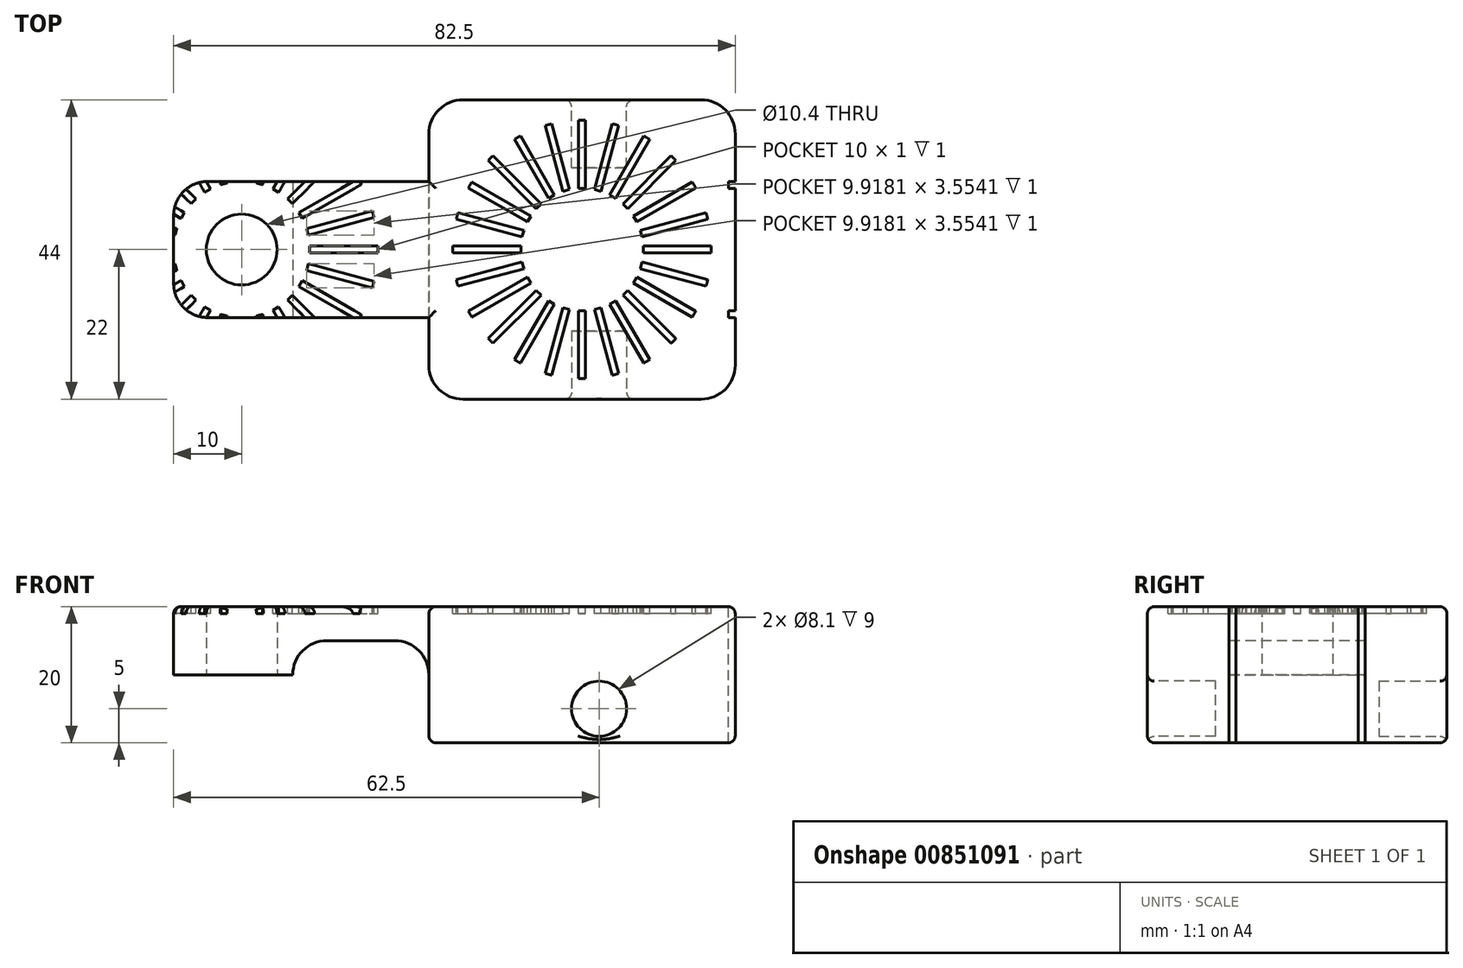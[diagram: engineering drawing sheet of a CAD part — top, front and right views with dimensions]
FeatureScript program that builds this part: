
annotation { "Feature Type Name" : "Feature", "Feature Type Description" : "" }
export const myFeature = defineFeature(function(context is Context, id is Id, definition is map)
    precondition{}
    {
        {
            var Q0;
            Q0=qCreatedBy(makeId("Top.planeOp"),FACE);
            var sketch = newSketch(context, id + "F0", { "sketchPlane" : qUnion([Q0])});
            skLineSegment(sketch, "E0.bottom", {"start": v(17.5, -22) * mm, "end": v(-17.5, -22) * mm});
            skLineSegment(sketch, "E0.top", {"start": v(17.5, 22) * mm, "end": v(-17.5, 22) * mm});
            skLineSegment(sketch, "E0.left", {"start": v(22.5, -17) * mm, "end": v(22.5, 17) * mm});
            skLineSegment(sketch, "E0.right", {"start": v(-22.5, -17) * mm, "end": v(-22.5, -10) * mm});
            skPoint(sketch, "E0.middle", {"position": v(0, 0) * mm});
            skPoint(sketch, "E1.visualSharp", {"position": v(-22.5, -22) * mm});
            skArc(sketch, "E1.filletArc", {"start": v(-22.5, -17) * mm, "mid": v(-21.04, -20.54) * mm, "end": v(-17.5, -22) * mm});
            skPoint(sketch, "E2.visualSharp", {"position": v(-22.5, 22) * mm});
            skArc(sketch, "E2.filletArc", {"start": v(-17.5, 22) * mm, "mid": v(-21.04, 20.54) * mm, "end": v(-22.5, 17) * mm});
            skPoint(sketch, "E3.visualSharp", {"position": v(22.5, 22) * mm});
            skArc(sketch, "E3.filletArc", {"start": v(22.5, 17) * mm, "mid": v(21.04, 20.54) * mm, "end": v(17.5, 22) * mm});
            skPoint(sketch, "E4.visualSharp", {"position": v(22.5, -22) * mm});
            skArc(sketch, "E4.filletArc", {"start": v(17.5, -22) * mm, "mid": v(21.04, -20.54) * mm, "end": v(22.5, -17) * mm});
            skLineSegment(sketch, "E5.bottom", {"start": v(-22.5, -10) * mm, "end": v(-55, -10) * mm});
            skLineSegment(sketch, "E5.top", {"start": v(-22.5, 10) * mm, "end": v(-55, 10) * mm});
            skLineSegment(sketch, "E5.right", {"start": v(-60, -5) * mm, "end": v(-60, 5) * mm});
            skCircle(sketch, "E6", {"center": v(-50, 0) * mm, "radius": 5.2 * mm});
            skPoint(sketch, "E7.orphan", {"position": v(0, -10) * mm});
            skLineSegment(sketch, "E8.trimOffspring", {"start": v(-22.5, 10) * mm, "end": v(-22.5, 17) * mm});
            skPoint(sketch, "E9.visualSharp", {"position": v(-60, -10) * mm});
            skArc(sketch, "E9.filletArc", {"start": v(-60, -5) * mm, "mid": v(-58.54, -8.54) * mm, "end": v(-55, -10) * mm});
            skPoint(sketch, "E10.visualSharp", {"position": v(-60, 10) * mm});
            skArc(sketch, "E10.filletArc", {"start": v(-55, 10) * mm, "mid": v(-58.54, 8.54) * mm, "end": v(-60, 5) * mm});
            skSolve(sketch);
        }
        {
            var Q0;
            Q0 = qSketchRegion(id + "F0", true);
            extrude(context, id + "F1", {"entities" : qUnion([Q0]), "depth" : 20 * mm, "offsetDistance" : 25 * mm});
        }
        {
            var Q0;
            Q0=makeQuery(id+"F1.opExtrude","CAP_FACE",FACE,{"disambiguationData":[OSD([sQuery(id+"F0.wireOp",EDGE,"E0.bottom"),sQuery(id+"F0.wireOp",EDGE,"E0.top"),sQuery(id+"F0.wireOp",EDGE,"E0.left"),sQuery(id+"F0.wireOp",EDGE,"E0.right"),sQuery(id+"F0.wireOp",EDGE,"E1.filletArc"),sQuery(id+"F0.wireOp",EDGE,"E2.filletArc"),sQuery(id+"F0.wireOp",EDGE,"E3.filletArc"),sQuery(id+"F0.wireOp",EDGE,"E4.filletArc"),sQuery(id+"F0.wireOp",EDGE,"E5.bottom"),sQuery(id+"F0.wireOp",EDGE,"E5.top"),sQuery(id+"F0.wireOp",EDGE,"E5.right"),sQuery(id+"F0.wireOp",EDGE,"E6"),sQuery(id+"F0.wireOp",EDGE,"E8.trimOffspring"),sQuery(id+"F0.wireOp",EDGE,"E9.filletArc"),sQuery(id+"F0.wireOp",EDGE,"E10.filletArc")])],"isStart":true});
            var sketch = newSketch(context, id + "F2", { "sketchPlane" : qUnion([Q0])});
            skLineSegment(sketch, "E11.bottom", {"start": v(-22.5, 10) * mm, "end": v(-60, 10) * mm});
            skLineSegment(sketch, "E11.top", {"start": v(-22.5, -10) * mm, "end": v(-60, -10) * mm});
            skLineSegment(sketch, "E11.left", {"start": v(-22.5, 10) * mm, "end": v(-22.5, -10) * mm});
            skLineSegment(sketch, "E11.right", {"start": v(-60, 10) * mm, "end": v(-60, -10) * mm});
            skSolve(sketch);
        }
        {
            var Q0;
            Q0 = qSketchRegion(id + "F2", true);
            extrude(context, id + "F3", {"entities" : qUnion([Q0]), "operationType" : NewBodyOperationType.REMOVE, "oppositeDirection" : true, "depth" : 10 * mm, "offsetDistance" : 25 * mm});
        }
        {
            var Q0;
            Q0=makeQuery(id+"F1.opExtrude","SWEPT_FACE",FACE,{"disambiguationData":[OSD([sQuery(id+"F0.wireOp",EDGE,"E0.bottom")])]});
            var sketch = newSketch(context, id + "F4", { "sketchPlane" : qUnion([Q0])});
            skCircle(sketch, "E12", {"center": v(2.5, 5) * mm, "radius": 4.05 * mm});
            skSolve(sketch);
        }
        {
            var Q0;
            Q0 = qSketchRegion(id + "F4", true);
            extrude(context, id + "F5", {"entities" : qUnion([Q0]), "operationType" : NewBodyOperationType.REMOVE, "oppositeDirection" : true, "depth" : 10 * mm, "offsetDistance" : 25 * mm});
        }
        {
            var Q0;
            Q0=makeQuery(id+"F1.opExtrude","SWEPT_FACE",FACE,{"disambiguationData":[OSD([sQuery(id+"F0.wireOp",EDGE,"E0.top")])]});
            var sketch = newSketch(context, id + "F6", { "sketchPlane" : qUnion([Q0])});
            skCircle(sketch, "E13", {"center": v(-2.5, 5) * mm, "radius": 4.05 * mm});
            skSolve(sketch);
        }
        {
            var Q0;
            Q0 = qSketchRegion(id + "F6", true);
            extrude(context, id + "F7", {"entities" : qUnion([Q0]), "operationType" : NewBodyOperationType.REMOVE, "oppositeDirection" : true, "depth" : 10 * mm, "offsetDistance" : 25 * mm});
        }
        {
            var Q0;
            Q0=makeQuery(id+"F1.opExtrude","CAP_FACE",FACE,{"disambiguationData":[OSD([sQuery(id+"F0.wireOp",EDGE,"E0.bottom"),sQuery(id+"F0.wireOp",EDGE,"E0.top"),sQuery(id+"F0.wireOp",EDGE,"E0.left"),sQuery(id+"F0.wireOp",EDGE,"E0.right"),sQuery(id+"F0.wireOp",EDGE,"E1.filletArc"),sQuery(id+"F0.wireOp",EDGE,"E2.filletArc"),sQuery(id+"F0.wireOp",EDGE,"E3.filletArc"),sQuery(id+"F0.wireOp",EDGE,"E4.filletArc"),sQuery(id+"F0.wireOp",EDGE,"E5.bottom"),sQuery(id+"F0.wireOp",EDGE,"E5.top"),sQuery(id+"F0.wireOp",EDGE,"E5.right"),sQuery(id+"F0.wireOp",EDGE,"E6"),sQuery(id+"F0.wireOp",EDGE,"E8.trimOffspring"),sQuery(id+"F0.wireOp",EDGE,"E9.filletArc"),sQuery(id+"F0.wireOp",EDGE,"E10.filletArc")])],"isStart":true});
            var Q1;
            Q1=makeQuery(id+"F3.boolean.opBoolean","COPY",EDGE,{"derivedFrom":makeQuery(id+"F3.opExtrude","CAP_EDGE",EDGE,{"disambiguationData":[OSD([sQuery(id+"F2.wireOp",EDGE,"E11.right")])],"isStart":false})});
            var Q2;
            Q2=makeQuery(id+"F1.opExtrude","CAP_EDGE",EDGE,{"disambiguationData":[OSD([sQuery(id+"F0.wireOp",EDGE,"E5.bottom")])],"isStart":false});
            var Q3;
            Q3=makeQuery(id+"F1.opExtrude","CAP_EDGE",EDGE,{"disambiguationData":[OSD([sQuery(id+"F0.wireOp",EDGE,"E0.top")])],"isStart":false});
            var Q4;
            Q4=makeQuery(id+"F1.opExtrude","SWEPT_FACE",FACE,{"disambiguationData":[OSD([sQuery(id+"F0.wireOp",EDGE,"E0.bottom")])]});
            var Q5;
            Q5=makeQuery(id+"F1.opExtrude","SWEPT_FACE",FACE,{"disambiguationData":[OSD([sQuery(id+"F0.wireOp",EDGE,"E0.top")])]});
            fillet(context, id + "F8", {"entities" : qUnion([Q0, Q1, Q2, Q3, Q4, Q5]), "radius" : 1 * mm, "tangentPropagation" : true, "allowEdgeOverflow" : false});
        }
        {
            var Q0;
            Q0=makeQuery(id+"F1.opExtrude","CAP_FACE",FACE,{"disambiguationData":[OSD([sQuery(id+"F0.wireOp",EDGE,"E0.bottom"),sQuery(id+"F0.wireOp",EDGE,"E0.top"),sQuery(id+"F0.wireOp",EDGE,"E0.left"),sQuery(id+"F0.wireOp",EDGE,"E0.right"),sQuery(id+"F0.wireOp",EDGE,"E1.filletArc"),sQuery(id+"F0.wireOp",EDGE,"E2.filletArc"),sQuery(id+"F0.wireOp",EDGE,"E3.filletArc"),sQuery(id+"F0.wireOp",EDGE,"E4.filletArc"),sQuery(id+"F0.wireOp",EDGE,"E5.bottom"),sQuery(id+"F0.wireOp",EDGE,"E5.top"),sQuery(id+"F0.wireOp",EDGE,"E5.right"),sQuery(id+"F0.wireOp",EDGE,"E6"),sQuery(id+"F0.wireOp",EDGE,"E8.trimOffspring"),sQuery(id+"F0.wireOp",EDGE,"E9.filletArc"),sQuery(id+"F0.wireOp",EDGE,"E10.filletArc")])],"isStart":false});
            var sketch = newSketch(context, id + "F9", { "sketchPlane" : qUnion([Q0])});
            skArc(sketch, "E14", {"start": v(19, -0.5) * mm, "mid": v(19, 0) * mm, "end": v(19, 0.5) * mm});
            skLineSegment(sketch, "E15.bottom", {"start": v(19, 0.5) * mm, "end": v(9, 0.5) * mm});
            skLineSegment(sketch, "E15.top", {"start": v(19, -0.5) * mm, "end": v(9, -0.5) * mm});
            skLineSegment(sketch, "E15.right", {"start": v(9, 0.5) * mm, "end": v(9, -0.5) * mm});
            skLineSegment(sketch, "E16.1.0", {"start": v(18.48, 4.43) * mm, "end": v(8.82, 1.84) * mm});
            skLineSegment(sketch, "E16.1.1", {"start": v(18.22, 5.4) * mm, "end": v(8.56, 2.81) * mm});
            skLineSegment(sketch, "E16.1.2", {"start": v(8.56, 2.81) * mm, "end": v(8.82, 1.84) * mm});
            skArc(sketch, "E16.1.3", {"start": v(18.48, 4.43) * mm, "mid": v(18.35, 4.92) * mm, "end": v(18.22, 5.4) * mm});
            skLineSegment(sketch, "E16.2.0", {"start": v(16.7, 9.06) * mm, "end": v(8.04, 4.06) * mm});
            skLineSegment(sketch, "E16.2.1", {"start": v(16.2, 9.93) * mm, "end": v(7.54, 4.93) * mm});
            skLineSegment(sketch, "E16.2.2", {"start": v(7.54, 4.93) * mm, "end": v(8.04, 4.06) * mm});
            skArc(sketch, "E16.2.3", {"start": v(16.7, 9.06) * mm, "mid": v(16.45, 9.5) * mm, "end": v(16.2, 9.93) * mm});
            skLineSegment(sketch, "E16.3.0", {"start": v(13.78, 13.08) * mm, "end": v(6.71, 6) * mm});
            skLineSegment(sketch, "E16.3.1", {"start": v(13.08, 13.78) * mm, "end": v(6, 6.71) * mm});
            skLineSegment(sketch, "E16.3.2", {"start": v(6, 6.71) * mm, "end": v(6.71, 6) * mm});
            skArc(sketch, "E16.3.3", {"start": v(13.78, 13.08) * mm, "mid": v(13.44, 13.44) * mm, "end": v(13.08, 13.78) * mm});
            skLineSegment(sketch, "E16.4.0", {"start": v(9.93, 16.2) * mm, "end": v(4.93, 7.54) * mm});
            skLineSegment(sketch, "E16.4.1", {"start": v(9.06, 16.7) * mm, "end": v(4.06, 8.04) * mm});
            skLineSegment(sketch, "E16.4.2", {"start": v(4.06, 8.04) * mm, "end": v(4.93, 7.54) * mm});
            skArc(sketch, "E16.4.3", {"start": v(9.93, 16.2) * mm, "mid": v(9.5, 16.45) * mm, "end": v(9.06, 16.7) * mm});
            skLineSegment(sketch, "E16.5.0", {"start": v(5.4, 18.22) * mm, "end": v(2.81, 8.56) * mm});
            skLineSegment(sketch, "E16.5.1", {"start": v(4.43, 18.48) * mm, "end": v(1.84, 8.82) * mm});
            skLineSegment(sketch, "E16.5.2", {"start": v(1.84, 8.82) * mm, "end": v(2.81, 8.56) * mm});
            skArc(sketch, "E16.5.3", {"start": v(5.4, 18.22) * mm, "mid": v(4.92, 18.35) * mm, "end": v(4.43, 18.48) * mm});
            skLineSegment(sketch, "E16.6.0", {"start": v(0.5, 19) * mm, "end": v(0.5, 9) * mm});
            skLineSegment(sketch, "E16.6.1", {"start": v(-0.5, 19) * mm, "end": v(-0.5, 9) * mm});
            skLineSegment(sketch, "E16.6.2", {"start": v(-0.5, 9) * mm, "end": v(0.5, 9) * mm});
            skArc(sketch, "E16.6.3", {"start": v(0.5, 19) * mm, "mid": v(0, 19) * mm, "end": v(-0.5, 19) * mm});
            skLineSegment(sketch, "E16.7.0", {"start": v(-4.43, 18.48) * mm, "end": v(-1.84, 8.82) * mm});
            skLineSegment(sketch, "E16.7.1", {"start": v(-5.4, 18.22) * mm, "end": v(-2.81, 8.56) * mm});
            skLineSegment(sketch, "E16.7.2", {"start": v(-2.81, 8.56) * mm, "end": v(-1.84, 8.82) * mm});
            skArc(sketch, "E16.7.3", {"start": v(-4.43, 18.48) * mm, "mid": v(-4.92, 18.35) * mm, "end": v(-5.4, 18.22) * mm});
            skLineSegment(sketch, "E16.8.0", {"start": v(-9.06, 16.7) * mm, "end": v(-4.06, 8.04) * mm});
            skLineSegment(sketch, "E16.8.1", {"start": v(-9.93, 16.2) * mm, "end": v(-4.93, 7.54) * mm});
            skLineSegment(sketch, "E16.8.2", {"start": v(-4.93, 7.54) * mm, "end": v(-4.06, 8.04) * mm});
            skArc(sketch, "E16.8.3", {"start": v(-9.06, 16.7) * mm, "mid": v(-9.5, 16.45) * mm, "end": v(-9.93, 16.2) * mm});
            skLineSegment(sketch, "E16.9.0", {"start": v(-13.08, 13.78) * mm, "end": v(-6, 6.71) * mm});
            skLineSegment(sketch, "E16.9.1", {"start": v(-13.78, 13.08) * mm, "end": v(-6.71, 6) * mm});
            skLineSegment(sketch, "E16.9.2", {"start": v(-6.71, 6) * mm, "end": v(-6, 6.71) * mm});
            skArc(sketch, "E16.9.3", {"start": v(-13.08, 13.78) * mm, "mid": v(-13.44, 13.44) * mm, "end": v(-13.78, 13.08) * mm});
            skLineSegment(sketch, "E16.10.0", {"start": v(-16.2, 9.93) * mm, "end": v(-7.54, 4.93) * mm});
            skLineSegment(sketch, "E16.10.1", {"start": v(-16.7, 9.06) * mm, "end": v(-8.04, 4.06) * mm});
            skLineSegment(sketch, "E16.10.2", {"start": v(-8.04, 4.06) * mm, "end": v(-7.54, 4.93) * mm});
            skArc(sketch, "E16.10.3", {"start": v(-16.2, 9.93) * mm, "mid": v(-16.45, 9.5) * mm, "end": v(-16.7, 9.06) * mm});
            skLineSegment(sketch, "E16.11.0", {"start": v(-18.22, 5.4) * mm, "end": v(-8.56, 2.81) * mm});
            skLineSegment(sketch, "E16.11.1", {"start": v(-18.48, 4.43) * mm, "end": v(-8.82, 1.84) * mm});
            skLineSegment(sketch, "E16.11.2", {"start": v(-8.82, 1.84) * mm, "end": v(-8.56, 2.81) * mm});
            skArc(sketch, "E16.11.3", {"start": v(-18.22, 5.4) * mm, "mid": v(-18.35, 4.92) * mm, "end": v(-18.48, 4.43) * mm});
            skLineSegment(sketch, "E16.12.0", {"start": v(-19, 0.5) * mm, "end": v(-9, 0.5) * mm});
            skLineSegment(sketch, "E16.12.1", {"start": v(-19, -0.5) * mm, "end": v(-9, -0.5) * mm});
            skLineSegment(sketch, "E16.12.2", {"start": v(-9, -0.5) * mm, "end": v(-9, 0.5) * mm});
            skArc(sketch, "E16.12.3", {"start": v(-19, 0.5) * mm, "mid": v(-19, 0) * mm, "end": v(-19, -0.5) * mm});
            skLineSegment(sketch, "E16.13.0", {"start": v(-18.48, -4.43) * mm, "end": v(-8.82, -1.84) * mm});
            skLineSegment(sketch, "E16.13.1", {"start": v(-18.22, -5.4) * mm, "end": v(-8.56, -2.81) * mm});
            skLineSegment(sketch, "E16.13.2", {"start": v(-8.56, -2.81) * mm, "end": v(-8.82, -1.84) * mm});
            skArc(sketch, "E16.13.3", {"start": v(-18.48, -4.43) * mm, "mid": v(-18.35, -4.92) * mm, "end": v(-18.22, -5.4) * mm});
            skLineSegment(sketch, "E16.14.0", {"start": v(-16.7, -9.06) * mm, "end": v(-8.04, -4.06) * mm});
            skLineSegment(sketch, "E16.14.1", {"start": v(-16.2, -9.93) * mm, "end": v(-7.54, -4.93) * mm});
            skLineSegment(sketch, "E16.14.2", {"start": v(-7.54, -4.93) * mm, "end": v(-8.04, -4.06) * mm});
            skArc(sketch, "E16.14.3", {"start": v(-16.7, -9.06) * mm, "mid": v(-16.45, -9.5) * mm, "end": v(-16.2, -9.93) * mm});
            skLineSegment(sketch, "E16.15.0", {"start": v(-13.78, -13.08) * mm, "end": v(-6.71, -6) * mm});
            skLineSegment(sketch, "E16.15.1", {"start": v(-13.08, -13.78) * mm, "end": v(-6, -6.71) * mm});
            skLineSegment(sketch, "E16.15.2", {"start": v(-6, -6.71) * mm, "end": v(-6.71, -6) * mm});
            skArc(sketch, "E16.15.3", {"start": v(-13.78, -13.08) * mm, "mid": v(-13.44, -13.44) * mm, "end": v(-13.08, -13.78) * mm});
            skLineSegment(sketch, "E16.16.0", {"start": v(-9.93, -16.2) * mm, "end": v(-4.93, -7.54) * mm});
            skLineSegment(sketch, "E16.16.1", {"start": v(-9.06, -16.7) * mm, "end": v(-4.06, -8.04) * mm});
            skLineSegment(sketch, "E16.16.2", {"start": v(-4.06, -8.04) * mm, "end": v(-4.93, -7.54) * mm});
            skArc(sketch, "E16.16.3", {"start": v(-9.93, -16.2) * mm, "mid": v(-9.5, -16.45) * mm, "end": v(-9.06, -16.7) * mm});
            skLineSegment(sketch, "E16.17.0", {"start": v(-5.4, -18.22) * mm, "end": v(-2.81, -8.56) * mm});
            skLineSegment(sketch, "E16.17.1", {"start": v(-4.43, -18.48) * mm, "end": v(-1.84, -8.82) * mm});
            skLineSegment(sketch, "E16.17.2", {"start": v(-1.84, -8.82) * mm, "end": v(-2.81, -8.56) * mm});
            skArc(sketch, "E16.17.3", {"start": v(-5.4, -18.22) * mm, "mid": v(-4.92, -18.35) * mm, "end": v(-4.43, -18.48) * mm});
            skLineSegment(sketch, "E16.18.0", {"start": v(-0.5, -19) * mm, "end": v(-0.5, -9) * mm});
            skLineSegment(sketch, "E16.18.1", {"start": v(0.5, -19) * mm, "end": v(0.5, -9) * mm});
            skLineSegment(sketch, "E16.18.2", {"start": v(0.5, -9) * mm, "end": v(-0.5, -9) * mm});
            skArc(sketch, "E16.18.3", {"start": v(-0.5, -19) * mm, "mid": v(0, -19) * mm, "end": v(0.5, -19) * mm});
            skLineSegment(sketch, "E16.19.0", {"start": v(4.43, -18.48) * mm, "end": v(1.84, -8.82) * mm});
            skLineSegment(sketch, "E16.19.1", {"start": v(5.4, -18.22) * mm, "end": v(2.81, -8.56) * mm});
            skLineSegment(sketch, "E16.19.2", {"start": v(2.81, -8.56) * mm, "end": v(1.84, -8.82) * mm});
            skArc(sketch, "E16.19.3", {"start": v(4.43, -18.48) * mm, "mid": v(4.92, -18.35) * mm, "end": v(5.4, -18.22) * mm});
            skLineSegment(sketch, "E16.20.0", {"start": v(9.06, -16.7) * mm, "end": v(4.06, -8.04) * mm});
            skLineSegment(sketch, "E16.20.1", {"start": v(9.93, -16.2) * mm, "end": v(4.93, -7.54) * mm});
            skLineSegment(sketch, "E16.20.2", {"start": v(4.93, -7.54) * mm, "end": v(4.06, -8.04) * mm});
            skArc(sketch, "E16.20.3", {"start": v(9.06, -16.7) * mm, "mid": v(9.5, -16.45) * mm, "end": v(9.93, -16.2) * mm});
            skLineSegment(sketch, "E16.21.0", {"start": v(13.08, -13.78) * mm, "end": v(6, -6.71) * mm});
            skLineSegment(sketch, "E16.21.1", {"start": v(13.78, -13.08) * mm, "end": v(6.71, -6) * mm});
            skLineSegment(sketch, "E16.21.2", {"start": v(6.71, -6) * mm, "end": v(6, -6.71) * mm});
            skArc(sketch, "E16.21.3", {"start": v(13.08, -13.78) * mm, "mid": v(13.44, -13.44) * mm, "end": v(13.78, -13.08) * mm});
            skLineSegment(sketch, "E16.22.0", {"start": v(16.2, -9.93) * mm, "end": v(7.54, -4.93) * mm});
            skLineSegment(sketch, "E16.22.1", {"start": v(16.7, -9.06) * mm, "end": v(8.04, -4.06) * mm});
            skLineSegment(sketch, "E16.22.2", {"start": v(8.04, -4.06) * mm, "end": v(7.54, -4.93) * mm});
            skArc(sketch, "E16.22.3", {"start": v(16.2, -9.93) * mm, "mid": v(16.45, -9.5) * mm, "end": v(16.7, -9.06) * mm});
            skLineSegment(sketch, "E16.23.0", {"start": v(18.22, -5.4) * mm, "end": v(8.56, -2.81) * mm});
            skLineSegment(sketch, "E16.23.1", {"start": v(18.48, -4.43) * mm, "end": v(8.82, -1.84) * mm});
            skLineSegment(sketch, "E16.23.2", {"start": v(8.82, -1.84) * mm, "end": v(8.56, -2.81) * mm});
            skArc(sketch, "E16.23.3", {"start": v(18.22, -5.4) * mm, "mid": v(18.35, -4.92) * mm, "end": v(18.48, -4.43) * mm});
            skSolve(sketch);
        }
        {
            var Q0;
            Q0 = qSketchRegion(id + "F9", true);
            extrude(context, id + "F10", {"entities" : qUnion([Q0]), "operationType" : NewBodyOperationType.REMOVE, "oppositeDirection" : true, "depth" : 1 * mm, "offsetDistance" : 25 * mm});
        }
        {
            var Q0;
            Q0=makeQuery(id+"F1.opExtrude","SWEPT_FACE",FACE,{"disambiguationData":[OSD([sQuery(id+"F0.wireOp",EDGE,"E5.bottom")])]});
            var sketch = newSketch(context, id + "F11", { "sketchPlane" : qUnion([Q0])});
            skLineSegment(sketch, "E17.bottom", {"start": v(-22.5, 15) * mm, "end": v(-42.5, 15) * mm});
            skLineSegment(sketch, "E17.top", {"start": v(-22.5, 10) * mm, "end": v(-42.5, 10) * mm});
            skLineSegment(sketch, "E17.left", {"start": v(-22.5, 15) * mm, "end": v(-22.5, 10) * mm});
            skLineSegment(sketch, "E17.right", {"start": v(-42.5, 15) * mm, "end": v(-42.5, 10) * mm});
            skSolve(sketch);
        }
        {
            var Q0;
            Q0 = qSketchRegion(id + "F11", true);
            extrude(context, id + "F12", {"entities" : qUnion([Q0]), "operationType" : NewBodyOperationType.REMOVE, "endBound" : BoundingType.THROUGH_ALL, "oppositeDirection" : true, "depth" : 25 * mm, "offsetDistance" : 25 * mm});
        }
        {
            var Q0;
            Q0=makeQuery(id+"F12.boolean.opBoolean","COPY",EDGE,{"derivedFrom":makeQuery(id+"F12.opExtrude","SWEPT_EDGE",EDGE,{"disambiguationData":[OSD([sQuery(id+"F11.wireOp",EDGE,"E17.bottom"),sQuery(id+"F11.wireOp",EDGE,"E17.right")])]})});
            var Q1;
            Q1=makeQuery(id+"F12.boolean.opBoolean","COPY",EDGE,{"derivedFrom":makeQuery(id+"F12.opExtrude","SWEPT_EDGE",EDGE,{"disambiguationData":[OSD([sQuery(id+"F0.wireOp",EDGE,"E0.right"),sQuery(id+"F0.wireOp",EDGE,"E5.bottom"),sQuery(id+"F11.wireOp",EDGE,"E17.bottom"),sQuery(id+"F11.wireOp",EDGE,"E17.left")])]})});
            fillet(context, id + "F13", {"entities" : qUnion([Q0, Q1]), "radius" : 5 * mm, "tangentPropagation" : true, "allowEdgeOverflow" : false});
        }
        {
            var Q0;
            Q0=makeQuery(id+"F1.opExtrude","CAP_FACE",FACE,{"disambiguationData":[OSD([sQuery(id+"F0.wireOp",EDGE,"E0.bottom"),sQuery(id+"F0.wireOp",EDGE,"E0.top"),sQuery(id+"F0.wireOp",EDGE,"E0.left"),sQuery(id+"F0.wireOp",EDGE,"E0.right"),sQuery(id+"F0.wireOp",EDGE,"E1.filletArc"),sQuery(id+"F0.wireOp",EDGE,"E2.filletArc"),sQuery(id+"F0.wireOp",EDGE,"E3.filletArc"),sQuery(id+"F0.wireOp",EDGE,"E4.filletArc"),sQuery(id+"F0.wireOp",EDGE,"E5.bottom"),sQuery(id+"F0.wireOp",EDGE,"E5.top"),sQuery(id+"F0.wireOp",EDGE,"E5.right"),sQuery(id+"F0.wireOp",EDGE,"E6"),sQuery(id+"F0.wireOp",EDGE,"E8.trimOffspring"),sQuery(id+"F0.wireOp",EDGE,"E9.filletArc"),sQuery(id+"F0.wireOp",EDGE,"E10.filletArc")])],"isStart":false});
            var sketch = newSketch(context, id + "F14", { "sketchPlane" : qUnion([Q0])});
            skLineSegment(sketch, "E18.bottom", {"start": v(-40, 0.5) * mm, "end": v(-30, 0.5) * mm});
            skLineSegment(sketch, "E18.top", {"start": v(-40, -0.5) * mm, "end": v(-30, -0.5) * mm});
            skLineSegment(sketch, "E18.left", {"start": v(-40, 0.5) * mm, "end": v(-40, -0.5) * mm});
            skLineSegment(sketch, "E18.right", {"start": v(-30, 0.5) * mm, "end": v(-30, -0.5) * mm});
            skPoint(sketch, "E19", {"position": v(-50, 0) * mm});
            skLineSegment(sketch, "E20.1.0", {"start": v(-40.47, 3.07) * mm, "end": v(-40.21, 2.1) * mm});
            skLineSegment(sketch, "E20.1.1", {"start": v(-30.81, 5.66) * mm, "end": v(-30.55, 4.7) * mm});
            skLineSegment(sketch, "E20.1.2", {"start": v(-40.47, 3.07) * mm, "end": v(-30.81, 5.66) * mm});
            skLineSegment(sketch, "E20.1.3", {"start": v(-40.21, 2.1) * mm, "end": v(-30.55, 4.7) * mm});
            skLineSegment(sketch, "E20.2.0", {"start": v(-41.59, 5.43) * mm, "end": v(-41.09, 4.57) * mm});
            skLineSegment(sketch, "E20.2.1", {"start": v(-32.93, 10.43) * mm, "end": v(-32.43, 9.57) * mm});
            skLineSegment(sketch, "E20.2.2", {"start": v(-41.59, 5.43) * mm, "end": v(-32.93, 10.43) * mm});
            skLineSegment(sketch, "E20.2.3", {"start": v(-41.09, 4.57) * mm, "end": v(-32.43, 9.57) * mm});
            skLineSegment(sketch, "E20.3.0", {"start": v(-43.28, 7.42) * mm, "end": v(-42.58, 6.72) * mm});
            skLineSegment(sketch, "E20.3.1", {"start": v(-36.21, 14.5) * mm, "end": v(-35.5, 13.79) * mm});
            skLineSegment(sketch, "E20.3.2", {"start": v(-43.28, 7.42) * mm, "end": v(-36.21, 14.5) * mm});
            skLineSegment(sketch, "E20.3.3", {"start": v(-42.58, 6.72) * mm, "end": v(-35.5, 13.79) * mm});
            skLineSegment(sketch, "E20.4.0", {"start": v(-45.43, 8.91) * mm, "end": v(-44.57, 8.41) * mm});
            skLineSegment(sketch, "E20.4.1", {"start": v(-40.43, 17.57) * mm, "end": v(-39.57, 17.07) * mm});
            skLineSegment(sketch, "E20.4.2", {"start": v(-45.43, 8.91) * mm, "end": v(-40.43, 17.57) * mm});
            skLineSegment(sketch, "E20.4.3", {"start": v(-44.57, 8.41) * mm, "end": v(-39.57, 17.07) * mm});
            skLineSegment(sketch, "E20.5.0", {"start": v(-47.9, 9.79) * mm, "end": v(-46.93, 9.53) * mm});
            skLineSegment(sketch, "E20.5.1", {"start": v(-45.3, 19.45) * mm, "end": v(-44.34, 19.19) * mm});
            skLineSegment(sketch, "E20.5.2", {"start": v(-47.9, 9.79) * mm, "end": v(-45.3, 19.45) * mm});
            skLineSegment(sketch, "E20.5.3", {"start": v(-46.93, 9.53) * mm, "end": v(-44.34, 19.19) * mm});
            skLineSegment(sketch, "E20.6.0", {"start": v(-50.5, 10) * mm, "end": v(-49.5, 10) * mm});
            skLineSegment(sketch, "E20.6.1", {"start": v(-50.5, 20) * mm, "end": v(-49.5, 20) * mm});
            skLineSegment(sketch, "E20.6.2", {"start": v(-50.5, 10) * mm, "end": v(-50.5, 20) * mm});
            skLineSegment(sketch, "E20.6.3", {"start": v(-49.5, 10) * mm, "end": v(-49.5, 20) * mm});
            skLineSegment(sketch, "E20.7.0", {"start": v(-53.07, 9.53) * mm, "end": v(-52.1, 9.79) * mm});
            skLineSegment(sketch, "E20.7.1", {"start": v(-55.66, 19.19) * mm, "end": v(-54.7, 19.45) * mm});
            skLineSegment(sketch, "E20.7.2", {"start": v(-53.07, 9.53) * mm, "end": v(-55.66, 19.19) * mm});
            skLineSegment(sketch, "E20.7.3", {"start": v(-52.1, 9.79) * mm, "end": v(-54.7, 19.45) * mm});
            skLineSegment(sketch, "E20.8.0", {"start": v(-55.43, 8.41) * mm, "end": v(-54.57, 8.91) * mm});
            skLineSegment(sketch, "E20.8.1", {"start": v(-60.43, 17.07) * mm, "end": v(-59.57, 17.57) * mm});
            skLineSegment(sketch, "E20.8.2", {"start": v(-55.43, 8.41) * mm, "end": v(-60.43, 17.07) * mm});
            skLineSegment(sketch, "E20.8.3", {"start": v(-54.57, 8.91) * mm, "end": v(-59.57, 17.57) * mm});
            skLineSegment(sketch, "E20.9.0", {"start": v(-57.42, 6.72) * mm, "end": v(-56.72, 7.42) * mm});
            skLineSegment(sketch, "E20.9.1", {"start": v(-64.5, 13.79) * mm, "end": v(-63.79, 14.5) * mm});
            skLineSegment(sketch, "E20.9.2", {"start": v(-57.42, 6.72) * mm, "end": v(-64.5, 13.79) * mm});
            skLineSegment(sketch, "E20.9.3", {"start": v(-56.72, 7.42) * mm, "end": v(-63.79, 14.5) * mm});
            skLineSegment(sketch, "E20.10.0", {"start": v(-58.91, 4.57) * mm, "end": v(-58.41, 5.43) * mm});
            skLineSegment(sketch, "E20.10.1", {"start": v(-67.57, 9.57) * mm, "end": v(-67.07, 10.43) * mm});
            skLineSegment(sketch, "E20.10.2", {"start": v(-58.91, 4.57) * mm, "end": v(-67.57, 9.57) * mm});
            skLineSegment(sketch, "E20.10.3", {"start": v(-58.41, 5.43) * mm, "end": v(-67.07, 10.43) * mm});
            skLineSegment(sketch, "E20.11.0", {"start": v(-59.79, 2.1) * mm, "end": v(-59.53, 3.07) * mm});
            skLineSegment(sketch, "E20.11.1", {"start": v(-69.45, 4.7) * mm, "end": v(-69.19, 5.66) * mm});
            skLineSegment(sketch, "E20.11.2", {"start": v(-59.79, 2.1) * mm, "end": v(-69.45, 4.7) * mm});
            skLineSegment(sketch, "E20.11.3", {"start": v(-59.53, 3.07) * mm, "end": v(-69.19, 5.66) * mm});
            skLineSegment(sketch, "E20.12.0", {"start": v(-60, -0.5) * mm, "end": v(-60, 0.5) * mm});
            skLineSegment(sketch, "E20.12.1", {"start": v(-70, -0.5) * mm, "end": v(-70, 0.5) * mm});
            skLineSegment(sketch, "E20.12.2", {"start": v(-60, -0.5) * mm, "end": v(-70, -0.5) * mm});
            skLineSegment(sketch, "E20.12.3", {"start": v(-60, 0.5) * mm, "end": v(-70, 0.5) * mm});
            skLineSegment(sketch, "E20.13.0", {"start": v(-59.53, -3.07) * mm, "end": v(-59.79, -2.1) * mm});
            skLineSegment(sketch, "E20.13.1", {"start": v(-69.19, -5.66) * mm, "end": v(-69.45, -4.7) * mm});
            skLineSegment(sketch, "E20.13.2", {"start": v(-59.53, -3.07) * mm, "end": v(-69.19, -5.66) * mm});
            skLineSegment(sketch, "E20.13.3", {"start": v(-59.79, -2.1) * mm, "end": v(-69.45, -4.7) * mm});
            skLineSegment(sketch, "E20.14.0", {"start": v(-58.41, -5.43) * mm, "end": v(-58.91, -4.57) * mm});
            skLineSegment(sketch, "E20.14.1", {"start": v(-67.07, -10.43) * mm, "end": v(-67.57, -9.57) * mm});
            skLineSegment(sketch, "E20.14.2", {"start": v(-58.41, -5.43) * mm, "end": v(-67.07, -10.43) * mm});
            skLineSegment(sketch, "E20.14.3", {"start": v(-58.91, -4.57) * mm, "end": v(-67.57, -9.57) * mm});
            skLineSegment(sketch, "E20.15.0", {"start": v(-56.72, -7.42) * mm, "end": v(-57.42, -6.72) * mm});
            skLineSegment(sketch, "E20.15.1", {"start": v(-63.79, -14.5) * mm, "end": v(-64.5, -13.79) * mm});
            skLineSegment(sketch, "E20.15.2", {"start": v(-56.72, -7.42) * mm, "end": v(-63.79, -14.5) * mm});
            skLineSegment(sketch, "E20.15.3", {"start": v(-57.42, -6.72) * mm, "end": v(-64.5, -13.79) * mm});
            skLineSegment(sketch, "E20.16.0", {"start": v(-54.57, -8.91) * mm, "end": v(-55.43, -8.41) * mm});
            skLineSegment(sketch, "E20.16.1", {"start": v(-59.57, -17.57) * mm, "end": v(-60.43, -17.07) * mm});
            skLineSegment(sketch, "E20.16.2", {"start": v(-54.57, -8.91) * mm, "end": v(-59.57, -17.57) * mm});
            skLineSegment(sketch, "E20.16.3", {"start": v(-55.43, -8.41) * mm, "end": v(-60.43, -17.07) * mm});
            skLineSegment(sketch, "E20.17.0", {"start": v(-52.1, -9.79) * mm, "end": v(-53.07, -9.53) * mm});
            skLineSegment(sketch, "E20.17.1", {"start": v(-54.7, -19.45) * mm, "end": v(-55.66, -19.19) * mm});
            skLineSegment(sketch, "E20.17.2", {"start": v(-52.1, -9.79) * mm, "end": v(-54.7, -19.45) * mm});
            skLineSegment(sketch, "E20.17.3", {"start": v(-53.07, -9.53) * mm, "end": v(-55.66, -19.19) * mm});
            skLineSegment(sketch, "E20.18.0", {"start": v(-49.5, -10) * mm, "end": v(-50.5, -10) * mm});
            skLineSegment(sketch, "E20.18.1", {"start": v(-49.5, -20) * mm, "end": v(-50.5, -20) * mm});
            skLineSegment(sketch, "E20.18.2", {"start": v(-49.5, -10) * mm, "end": v(-49.5, -20) * mm});
            skLineSegment(sketch, "E20.18.3", {"start": v(-50.5, -10) * mm, "end": v(-50.5, -20) * mm});
            skLineSegment(sketch, "E20.19.0", {"start": v(-46.93, -9.53) * mm, "end": v(-47.9, -9.79) * mm});
            skLineSegment(sketch, "E20.19.1", {"start": v(-44.34, -19.19) * mm, "end": v(-45.3, -19.45) * mm});
            skLineSegment(sketch, "E20.19.2", {"start": v(-46.93, -9.53) * mm, "end": v(-44.34, -19.19) * mm});
            skLineSegment(sketch, "E20.19.3", {"start": v(-47.9, -9.79) * mm, "end": v(-45.3, -19.45) * mm});
            skLineSegment(sketch, "E20.20.0", {"start": v(-44.57, -8.41) * mm, "end": v(-45.43, -8.91) * mm});
            skLineSegment(sketch, "E20.20.1", {"start": v(-39.57, -17.07) * mm, "end": v(-40.43, -17.57) * mm});
            skLineSegment(sketch, "E20.20.2", {"start": v(-44.57, -8.41) * mm, "end": v(-39.57, -17.07) * mm});
            skLineSegment(sketch, "E20.20.3", {"start": v(-45.43, -8.91) * mm, "end": v(-40.43, -17.57) * mm});
            skLineSegment(sketch, "E20.21.0", {"start": v(-42.58, -6.72) * mm, "end": v(-43.28, -7.42) * mm});
            skLineSegment(sketch, "E20.21.1", {"start": v(-35.5, -13.79) * mm, "end": v(-36.21, -14.5) * mm});
            skLineSegment(sketch, "E20.21.2", {"start": v(-42.58, -6.72) * mm, "end": v(-35.5, -13.79) * mm});
            skLineSegment(sketch, "E20.21.3", {"start": v(-43.28, -7.42) * mm, "end": v(-36.21, -14.5) * mm});
            skLineSegment(sketch, "E20.22.0", {"start": v(-41.09, -4.57) * mm, "end": v(-41.59, -5.43) * mm});
            skLineSegment(sketch, "E20.22.1", {"start": v(-32.43, -9.57) * mm, "end": v(-32.93, -10.43) * mm});
            skLineSegment(sketch, "E20.22.2", {"start": v(-41.09, -4.57) * mm, "end": v(-32.43, -9.57) * mm});
            skLineSegment(sketch, "E20.22.3", {"start": v(-41.59, -5.43) * mm, "end": v(-32.93, -10.43) * mm});
            skLineSegment(sketch, "E20.23.0", {"start": v(-40.21, -2.1) * mm, "end": v(-40.47, -3.07) * mm});
            skLineSegment(sketch, "E20.23.1", {"start": v(-30.55, -4.7) * mm, "end": v(-30.81, -5.66) * mm});
            skLineSegment(sketch, "E20.23.2", {"start": v(-40.21, -2.1) * mm, "end": v(-30.55, -4.7) * mm});
            skLineSegment(sketch, "E20.23.3", {"start": v(-40.47, -3.07) * mm, "end": v(-30.81, -5.66) * mm});
            skSolve(sketch);
        }
        {
            var Q0;
            Q0 = qSketchRegion(id + "F14", true);
            extrude(context, id + "F15", {"entities" : qUnion([Q0]), "operationType" : NewBodyOperationType.REMOVE, "oppositeDirection" : true, "depth" : 1 * mm, "offsetDistance" : 25 * mm});
        }
        {
            var Q0;
            Q0=makeQuery(id+"F1.opExtrude","CAP_FACE",FACE,{"disambiguationData":[OSD([sQuery(id+"F0.wireOp",EDGE,"E0.bottom"),sQuery(id+"F0.wireOp",EDGE,"E0.top"),sQuery(id+"F0.wireOp",EDGE,"E0.left"),sQuery(id+"F0.wireOp",EDGE,"E0.right"),sQuery(id+"F0.wireOp",EDGE,"E1.filletArc"),sQuery(id+"F0.wireOp",EDGE,"E2.filletArc"),sQuery(id+"F0.wireOp",EDGE,"E3.filletArc"),sQuery(id+"F0.wireOp",EDGE,"E4.filletArc"),sQuery(id+"F0.wireOp",EDGE,"E5.bottom"),sQuery(id+"F0.wireOp",EDGE,"E5.top"),sQuery(id+"F0.wireOp",EDGE,"E5.right"),sQuery(id+"F0.wireOp",EDGE,"E6"),sQuery(id+"F0.wireOp",EDGE,"E8.trimOffspring"),sQuery(id+"F0.wireOp",EDGE,"E9.filletArc"),sQuery(id+"F0.wireOp",EDGE,"E10.filletArc")])],"isStart":false});
            var sketch = newSketch(context, id + "F16", { "sketchPlane" : qUnion([Q0])});
            skLineSegment(sketch, "E21.bottom", {"start": v(21.5, 10) * mm, "end": v(23.5, 10) * mm});
            skLineSegment(sketch, "E21.top", {"start": v(21.5, 9) * mm, "end": v(23.5, 9) * mm});
            skLineSegment(sketch, "E21.left", {"start": v(21.5, 10) * mm, "end": v(21.5, 9) * mm});
            skLineSegment(sketch, "E21.right", {"start": v(23.5, 10) * mm, "end": v(23.5, 9) * mm});
            skLineSegment(sketch, "E22.bottom", {"start": v(21.5, -9) * mm, "end": v(23.5, -9) * mm});
            skLineSegment(sketch, "E22.top", {"start": v(21.5, -10) * mm, "end": v(23.5, -10) * mm});
            skLineSegment(sketch, "E22.left", {"start": v(21.5, -9) * mm, "end": v(21.5, -10) * mm});
            skLineSegment(sketch, "E22.right", {"start": v(23.5, -9) * mm, "end": v(23.5, -10) * mm});
            skSolve(sketch);
        }
        {
            var Q0;
            Q0 = qSketchRegion(id + "F16", true);
            extrude(context, id + "F17", {"entities" : qUnion([Q0]), "operationType" : NewBodyOperationType.REMOVE, "endBound" : BoundingType.THROUGH_ALL, "oppositeDirection" : true, "depth" : 25 * mm, "offsetDistance" : 25 * mm});
        }
    });
